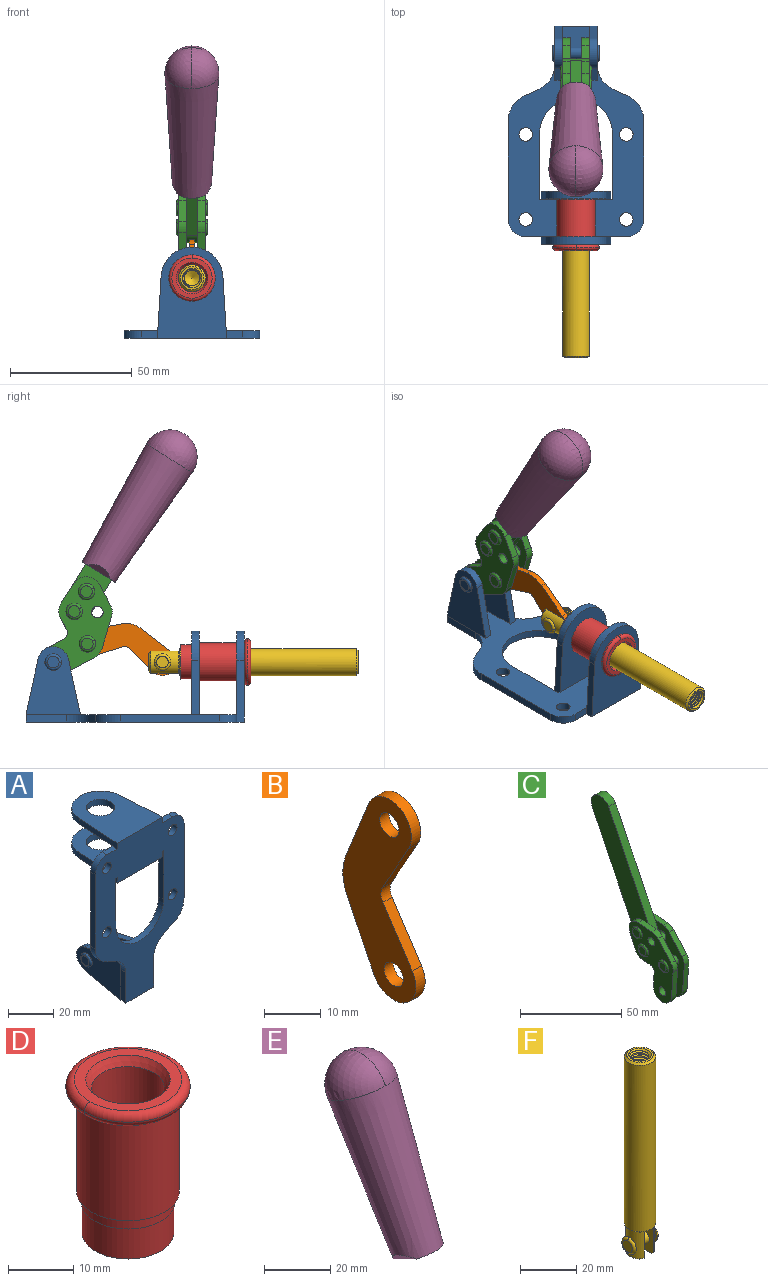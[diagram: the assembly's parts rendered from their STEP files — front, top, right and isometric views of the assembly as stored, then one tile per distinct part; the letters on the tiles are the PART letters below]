
ASSEMBLY  parts=6 mates=6
PART A: 55 faces, bbox 55.7x37.4x89.8 mm
  f0: torus R=2.41mm, axis (-1,0,0), area 15mm2, adj f11,f15,f25
  f1: torus R=2.41mm, axis (-1,0,0), area 15mm2, adj f10,f12,f22
  f2: cylinder r=2.78mm len=5.56mm, axis (0,-1,0), area 54.2mm2, adj f30,f54
  f3: cylinder r=14.99mm len=29.97mm, axis (0,-1,0), area 145.9mm2, adj f30,f49,f53,f54
  f4: cylinder r=2.78mm len=5.56mm, axis (0,-1,0), area 54.2mm2, adj f30,f54
  f5: cylinder r=2.78mm len=5.56mm, axis (0,-1,0), area 54.2mm2, adj f30,f54
  f6: cylinder r=2.78mm len=5.56mm, axis (0,-1,0), area 54.2mm2, adj f30,f54
  f7: cylinder r=6.35mm len=12.7mm, axis (0,0,1), area 123.6mm2, adj f27,f51
  f8: cylinder r=6.35mm len=12.7mm, axis (0,0,-1), area 124.7mm2, adj f21,f35
  f9: cylinder r=2.41mm len=11.18mm, axis (-1,0,0), area 169.4mm2, adj f16,f19
  f10: plane 4.83x4.83mm, normal (1,0,0), area 18.3mm2, adj f1,f12
  f11: plane 4.83x4.83mm, normal (-1,0,0), area 18.3mm2, adj f0,f15
  f12: torus R=2.41mm, axis (-1,0,0), area 15mm2, adj f1,f10,f22
  f13: cylinder r=6.35mm len=12.41mm, axis (1,0,0), area 53.4mm2, adj f18,f19,f22,f23
  f14: cylinder r=6.35mm len=12.41mm, axis (-1,0,0), area 53.4mm2, adj f16,f17,f24,f25
  f15: torus R=2.41mm, axis (-1,0,0), area 15mm2, adj f0,f11,f25
  f16: plane 27.86x22.35mm, normal (1,0,0), area 425.4mm2, adj f9,f14,f17,f24,f30
  f17: plane 22.86x4.97mm, normal (0,0.21,0.98), area 72.5mm2, adj f14,f16,f25,f30
  f18: plane 22.86x4.97mm, normal (0,0.21,0.98), area 72.5mm2, adj f13,f19,f22,f30
  f19: plane 27.86x22.35mm, normal (-1,0,0), area 425.4mm2, adj f9,f13,f18,f23,f30
  f20: cylinder r=12.7mm len=25.35mm, axis (0,0,-1), area 119.8mm2, adj f21,f34,f35,f36
  f21: plane 34.21x28.07mm, normal (0,0,-1), area 702.4mm2, adj f8,f20,f30,f34,f36
  f22: plane 27.96x22.45mm, normal (1,0,0), area 407.2mm2, adj f1,f12,f13,f18,f23,f30,f42,f43
  f23: plane 22.86x4.97mm, normal (0,0.21,-0.98), area 72.5mm2, adj f13,f19,f22,f44
  f24: plane 22.86x4.97mm, normal (0,0.21,-0.98), area 72.5mm2, adj f14,f16,f25,f44
  f25: plane 27.86x22.35mm, normal (-1,0,0), area 407.1mm2, adj f0,f14,f15,f17,f24,f30,f45,f46
  f26: plane 3.1x0.95mm, normal (0,0,-1), area 2.7mm2, adj f30,f49,f50,f54
  f27: plane 34.21x28.07mm, normal (0,0,1), area 702.4mm2, adj f7,f28,f30,f50,f52
  f28: cylinder r=12.7mm len=25.35mm, axis (0,0,1), area 118.8mm2, adj f27,f50,f51,f52
  f29: plane 3.1x0.95mm, normal (0,0,-1), area 2.7mm2, adj f30,f52,f53,f54
  f30: plane 86.54x55.63mm, normal (0,1,0), area 2362.9mm2, adj f2,f3,f4,f5,f6,f16,f17,f18
  f31: plane 40.56x3.1mm, normal (-1,0,0), area 125.7mm2, adj f30,f32,f48,f54
  f32: cylinder r=7.11mm len=7.11mm, axis (0,-1,0), area 34.6mm2, adj f30,f31,f33,f54
  f33: plane 6.67x3.1mm, normal (0,0,1), area 20.4mm2, adj f30,f32,f34,f54
  f34: plane 25.39x3.13mm, normal (-1,0.06,0), area 79.5mm2, adj f20,f21,f33,f35,f54
  f35: plane 37.31x28.45mm, normal (0,0,1), area 789.9mm2, adj f8,f20,f34,f36,f54
  f36: plane 25.39x3.13mm, normal (1,0.06,0), area 79.5mm2, adj f20,f21,f35,f37,f54
  f37: plane 6.67x3.1mm, normal (0,0,1), area 20.4mm2, adj f30,f36,f38,f54
  f38: cylinder r=7.11mm len=7.11mm, axis (0,-1,0), area 34.6mm2, adj f30,f37,f39,f54
  f39: plane 40.56x3.1mm, normal (1,0,0), area 125.7mm2, adj f30,f38,f40,f54
  f40: cylinder r=11.18mm len=10.16mm, axis (0,-1,0), area 39.5mm2, adj f30,f39,f41,f54
  f41: plane 6.09x3.1mm, normal (0.42,0,-0.91), area 20.8mm2, adj f30,f40,f42,f54
  f42: cylinder r=11.18mm len=9.41mm, axis (0,-1,0), area 37.2mm2, adj f22,f30,f41,f43,f54
  f43: plane 16.5x3.1mm, normal (1,0,0), area 51.1mm2, adj f22,f42,f44,f54
  f44: plane 17.37x3.1mm, normal (0,0,-1), area 53.8mm2, adj f23,f24,f30,f43,f45,f54
  f45: plane 16.5x3.1mm, normal (-1,0,0), area 51.1mm2, adj f25,f44,f46,f54
  f46: cylinder r=11.18mm len=9.41mm, axis (0,-1,0), area 37.2mm2, adj f25,f30,f45,f47,f54
  f47: plane 6.09x3.1mm, normal (-0.42,0,-0.91), area 20.8mm2, adj f30,f46,f48,f54
  f48: cylinder r=11.18mm len=10.16mm, axis (0,-1,0), area 39.5mm2, adj f30,f31,f47,f54
  f49: plane 26.54x3.1mm, normal (-1,0,0), area 82.3mm2, adj f3,f26,f30,f54
  f50: plane 25.39x3.1mm, normal (1,0.06,0), area 78.8mm2, adj f26,f27,f28,f51,f54
  f51: plane 37.31x28.45mm, normal (0,0,-1), area 789.9mm2, adj f7,f28,f50,f52,f54
  f52: plane 25.39x3.1mm, normal (-1,0.06,0), area 78.8mm2, adj f27,f28,f29,f51,f54
  f53: plane 26.54x3.1mm, normal (1,0,0), area 82.3mm2, adj f3,f29,f30,f54
  f54: plane 89.66x55.63mm, normal (0,-1,0), area 2678.5mm2, adj f2,f3,f4,f5,f6,f26,f29,f31
PART B: 12 faces, bbox 2.3x18.2x42.8 mm
  f0: cylinder r=2.4mm len=4.8mm, axis (1,0,0), area 34.9mm2, adj f4,f11
  f1: cylinder r=10.41mm len=8.47mm, axis (1,0,0), area 20.2mm2, adj f4,f9,f10,f11
  f2: cylinder r=3.05mm len=3.16mm, axis (1,0,0), area 7.7mm2, adj f4,f6,f7,f11
  f3: cylinder r=2.4mm len=4.8mm, axis (1,0,0), area 34.9mm2, adj f4,f11
  f4: plane 42.81x18.23mm, normal (-1,0,0), area 414.1mm2, adj f0,f1,f2,f3,f5,f6,f7,f8
  f5: cylinder r=5.54mm len=10.67mm, axis (1,0,0), area 41.8mm2, adj f4,f6,f10,f11
  f6: plane 11.66x6.53mm, normal (0,-0.87,-0.49), area 30.9mm2, adj f2,f4,f5,f11
  f7: plane 11.17x7.33mm, normal (0,-0.84,0.55), area 30.9mm2, adj f2,f4,f8,f11
  f8: cylinder r=5.54mm len=10.51mm, axis (1,0,0), area 41.8mm2, adj f4,f7,f9,f11
  f9: plane 13.67x6.67mm, normal (0,0.9,-0.44), area 35.1mm2, adj f1,f4,f8,f11
  f10: plane 14.1x5.7mm, normal (0,0.93,0.37), area 35.1mm2, adj f1,f4,f5,f11
  f11: plane 42.81x18.23mm, normal (1,0,0), area 414.1mm2, adj f0,f1,f2,f3,f5,f6,f7,f8
PART C: 59 faces, bbox 12.9x60.2x99.6 mm
  f0: torus R=2.39mm, axis (-1,0,0), area 14.9mm2, adj f20,f43,f51
  f1: torus R=2.39mm, axis (-1,0,0), area 14.9mm2, adj f19,f42,f51
  f2: torus R=2.39mm, axis (-1,0,0), area 14.9mm2, adj f18,f35,f51
  f3: torus R=2.39mm, axis (-1,0,0), area 14.9mm2, adj f14,f17,f23
  f4: torus R=2.39mm, axis (-1,0,0), area 14.9mm2, adj f13,f16,f23
  f5: torus R=2.39mm, axis (-1,0,0), area 14.9mm2, adj f12,f15,f23
  f6: cylinder r=2.39mm len=4.78mm, axis (1,0,0), area 46.5mm2, adj f48,f50,f51
  f7: cylinder r=2.39mm len=4.78mm, axis (1,0,0), area 46.5mm2, adj f50,f51
  f8: cylinder r=6.35mm len=12.68mm, axis (1,0,0), area 61.8mm2, adj f38,f39,f50,f51
  f9: cylinder r=2.39mm len=4.78mm, axis (-1,0,0), area 70.5mm2, adj f46,f50
  f10: cylinder r=2.39mm len=4.78mm, axis (-1,0,0), area 46.5mm2, adj f23,f45,f46
  f11: cylinder r=2.39mm len=4.78mm, axis (-1,0,0), area 46.5mm2, adj f23,f46
  f12: plane 4.78x4.78mm, normal (1,0,0), area 17.9mm2, adj f5,f15
  f13: plane 4.78x4.78mm, normal (1,0,0), area 17.9mm2, adj f4,f16
  f14: plane 4.78x4.78mm, normal (1,0,0), area 17.9mm2, adj f3,f17
  f15: torus R=2.39mm, axis (-1,0,0), area 14.9mm2, adj f5,f12,f23
  f16: torus R=2.39mm, axis (-1,0,0), area 14.9mm2, adj f4,f13,f23
  f17: torus R=2.39mm, axis (-1,0,0), area 14.9mm2, adj f3,f14,f23
  f18: plane 4.78x4.78mm, normal (-1,0,0), area 17.9mm2, adj f2,f35
  f19: plane 4.78x4.78mm, normal (-1,0,0), area 17.9mm2, adj f1,f42
  f20: plane 4.78x4.78mm, normal (-1,0,0), area 17.9mm2, adj f0,f43
  f21: plane 2.26x0.2mm, normal (1,0,0), area 0.2mm2, adj f31,f44
  f22: plane 2.26x0.2mm, normal (-1,0,0), area 0.2mm2, adj f41,f44
  f23: plane 39.37x30.77mm, normal (1,0,0), area 565.5mm2, adj f3,f4,f5,f10,f11,f15,f16,f17
  f24: cylinder r=6.1mm len=4.15mm, axis (-1,0,0), area 14.7mm2, adj f23,f25,f32,f46
  f25: plane 10.25x9.01mm, normal (0,-0.75,0.66), area 42.3mm2, adj f23,f24,f26,f46
  f26: cylinder r=6.35mm len=4.64mm, axis (-1,0,0), area 15.6mm2, adj f23,f25,f27,f46
  f27: plane 15.84x3.1mm, normal (0,-1,-0.07), area 49.2mm2, adj f23,f26,f28,f46
  f28: cylinder r=6.35mm len=12.68mm, axis (-1,0,0), area 61.8mm2, adj f23,f27,f29,f46
  f29: plane 8.11x3.1mm, normal (0,1,0.07), area 25.2mm2, adj f23,f28,f30,f46
  f30: cylinder r=3.05mm len=3.25mm, axis (-1,0,0), area 14.8mm2, adj f23,f29,f31,f46
  f31: plane 5.99x3.1mm, normal (0,0.07,-1), area 18.6mm2, adj f21,f23,f30,f44,f46
  f32: plane 9.5x3.1mm, normal (0,-0.07,1), area 29.5mm2, adj f23,f24,f33,f46,f47
  f33: cylinder r=6.1mm len=8.63mm, axis (-1,0,0), area 39.1mm2, adj f23,f32,f34,f47
  f34: plane 8.65x3.96mm, normal (0,0.91,-0.42), area 29.5mm2, adj f23,f33,f44,f47
  f35: torus R=2.39mm, axis (-1,0,0), area 14.9mm2, adj f2,f18,f51
  f36: plane 10.25x9.01mm, normal (0,-0.75,0.66), area 42.3mm2, adj f37,f49,f50,f51
  f37: cylinder r=6.35mm len=4.64mm, axis (1,0,0), area 15.6mm2, adj f36,f38,f50,f51
  f38: plane 15.84x3.1mm, normal (0,-1,-0.07), area 49.2mm2, adj f8,f37,f50,f51
  f39: plane 8.11x3.1mm, normal (0,1,0.07), area 25.2mm2, adj f8,f40,f50,f51
  f40: cylinder r=3.05mm len=3.25mm, axis (1,0,0), area 14.8mm2, adj f39,f41,f50,f51
  f41: plane 5.99x3.1mm, normal (0,0.07,-1), area 18.6mm2, adj f22,f40,f44,f50,f51
  f42: torus R=2.39mm, axis (-1,0,0), area 14.9mm2, adj f1,f19,f51
  f43: torus R=2.39mm, axis (-1,0,0), area 14.9mm2, adj f0,f20,f51
  f44: cylinder r=6.35mm len=12.12mm, axis (-1,0,0), area 128.9mm2, adj f21,f22,f23,f31,f34,f41,f46,f47
  f45: plane 2.65x1.35mm, normal (1,0,0), area 1mm2, adj f10,f55
  f46: plane 39.08x20.42mm, normal (-1,0,0), area 412.5mm2, adj f9,f10,f11,f24,f25,f26,f27,f28
  f47: plane 77.62x39.82mm, normal (1,0,0), area 850mm2, adj f32,f33,f34,f44,f53,f54,f55
  f48: plane 2.65x1.35mm, normal (-1,0,0), area 1mm2, adj f6,f55
  f49: cylinder r=6.1mm len=4.15mm, axis (1,0,0), area 14.7mm2, adj f36,f50,f51,f56
  f50: plane 39.08x20.42mm, normal (1,0,0), area 412.5mm2, adj f6,f7,f8,f9,f36,f37,f38,f39
  f51: plane 39.37x30.77mm, normal (-1,0,0), area 565.5mm2, adj f0,f1,f2,f6,f7,f8,f35,f36
  f52: plane 8.65x3.96mm, normal (0,0.91,-0.42), area 29.5mm2, adj f44,f51,f57,f58
  f53: plane 68.49x33.4mm, normal (0,0.9,-0.44), area 358.1mm2, adj f44,f47,f54,f58
  f54: cylinder r=6.35mm len=12.06mm, axis (1,0,0), area 93.7mm2, adj f47,f53,f55,f58
  f55: plane 68.49x33.4mm, normal (0,-0.9,0.44), area 358.1mm2, adj f44,f45,f46,f47,f48,f50,f54,f58
  f56: plane 9.5x3.1mm, normal (0,-0.07,1), area 29.5mm2, adj f49,f50,f51,f57,f58
  f57: cylinder r=6.1mm len=8.63mm, axis (1,0,0), area 39.1mm2, adj f51,f52,f56,f58
  f58: plane 77.62x39.82mm, normal (-1,0,0), area 850mm2, adj f44,f52,f53,f54,f55,f56,f57
PART D: 15 faces, bbox 20.6x20.6x28.7 mm
  f0: torus R=8.26mm, axis (0,0,1), area 56.8mm2, adj f1,f10,f12
  f1: torus R=8.26mm, axis (0,0,1), area 56.8mm2, adj f0,f6,f13
  f2: cylinder r=5.59mm len=25.91mm, axis (0,0,1), area 909.6mm2, adj f3,f4
  f3: cone r=6.86mm half-angle=45deg, axis (0,0,-1), area 70.2mm2, adj f2,f14
  f4: cone r=6.47mm half-angle=30deg, axis (0,0,1), area 66.7mm2, adj f2,f13
  f5: cylinder r=7.04mm len=14.07mm, axis (0,0,1), area 252.6mm2, adj f11,f14
  f6: torus R=8.26mm, axis (0,0,1), area 56.8mm2, adj f1,f12,f13
  f7: cylinder r=7.16mm len=14.33mm, axis (0,0,1), area 91.5mm2, adj f9,f11
  f8: cylinder r=7.86mm len=18.42mm, axis (0,0,1), area 909.6mm2, adj f9,f10
  f9: plane 15.72x15.72mm, normal (0,0,-1), area 33mm2, adj f7,f8
  f10: plane 16.51x16.51mm, normal (0,0,-1), area 19.9mm2, adj f0,f8,f12
  f11: plane 14.33x14.33mm, normal (0,0,-1), area 5.7mm2, adj f5,f7
  f12: torus R=8.26mm, axis (0,0,1), area 56.8mm2, adj f0,f6,f10
  f13: plane 16.51x16.51mm, normal (0,0,1), area 82.7mm2, adj f1,f4,f6
  f14: plane 14.07x14.07mm, normal (0,0,-1), area 7.8mm2, adj f3,f5
PART E: 11 faces, bbox 22.3x42.6x64.5 mm
  f0: sphere r=11.13mm, area 411.4mm2, adj f1,f8
  f1: cone r=11.11mm half-angle=3.3deg, axis (0,0.44,0.9), area 3251.8mm2, adj f0,f7,f8,f9,f10
  f2: cylinder r=6.16mm len=11.7mm, axis (1,0,0), area 89.5mm2, adj f3,f4,f5,f6
  f3: plane 60.23x36.75mm, normal (-1,0,0), area 763.6mm2, adj f2,f4,f6,f10
  f4: plane 51.37x25.05mm, normal (0,0.9,-0.44), area 264.2mm2, adj f2,f3,f5,f10
  f5: plane 60.23x36.75mm, normal (1,0,0), area 763.6mm2, adj f2,f4,f6,f10
  f6: plane 51.37x25.05mm, normal (0,-0.9,0.44), area 264.2mm2, adj f2,f3,f5,f10
  f7: plane 9.95x5.95mm, normal (0.71,-0.31,-0.64), area 25.8mm2, adj f1,f10
  f8: sphere r=11.13mm, area 411.4mm2, adj f0,f1
  f9: plane 9.95x5.95mm, normal (-0.71,-0.31,-0.64), area 25.8mm2, adj f1,f10
  f10: plane 14.27x11.38mm, normal (0,-0.44,-0.9), area 106.7mm2, adj f1,f3,f4,f5,f6,f7,f9
PART F: 48 faces, bbox 12.6x11.1x86.1 mm
  f0: torus R=2.41mm, axis (-1,0,0), area 15mm2, adj f30,f32,f34
  f1: torus R=2.41mm, axis (-1,0,0), area 15mm2, adj f29,f31,f33
  f2: cylinder r=5.54mm len=72.39mm, axis (0,0,1), area 2518.5mm2, adj f3,f4,f42,f43
  f3: cone r=5.54mm half-angle=45deg, axis (0,0,1), area 7.6mm2, adj f2,f5,f41
  f4: cone r=5.54mm half-angle=45deg, axis (0,0,-1), area 34.9mm2, adj f2,f39
  f5: cylinder r=5.08mm len=11.48mm, axis (0,0,1), area 108.3mm2, adj f3,f7,f8,f41
  f6: cylinder r=2.41mm len=4.83mm, axis (-1,0,0), area 71.2mm2, adj f40,f41
  f7: cylinder r=2.41mm len=4.83mm, axis (-1,0,0), area 7.6mm2, adj f5,f34
  f8: cone r=5.08mm half-angle=45deg, axis (0,0,1), area 10.6mm2, adj f5,f37,f41
  f9: cone r=3.98mm half-angle=45deg, axis (0,0,1), area 17.6mm2, adj f27,f39,f45,f46,f47
  f10: cylinder r=2.41mm len=4.83mm, axis (-1,0,0), area 7.6mm2, adj f33,f38
  f11: cylinder r=3.2mm len=6.4mm, axis (0,0,1), area 78.4mm2, adj f12,f28,f44,f45,f47
  f12: cylinder r=3.2mm len=6.4mm, axis (0,0,1), area 10.5mm2, adj f11,f13,f45,f47
  f13: cylinder r=3.2mm len=6.4mm, axis (0,0,1), area 10.5mm2, adj f12,f14,f45,f47
  f14: cylinder r=3.2mm len=6.4mm, axis (0,0,1), area 10.5mm2, adj f13,f15,f45,f47
  f15: cylinder r=3.2mm len=6.4mm, axis (0,0,1), area 10.5mm2, adj f14,f16,f45,f47
  f16: cylinder r=3.2mm len=6.4mm, axis (0,0,1), area 10.5mm2, adj f15,f17,f45,f47
  f17: cylinder r=3.2mm len=6.4mm, axis (0,0,1), area 10.5mm2, adj f16,f18,f45,f47
  f18: cylinder r=3.2mm len=6.4mm, axis (0,0,1), area 10.5mm2, adj f17,f19,f45,f47
  f19: cylinder r=3.2mm len=6.4mm, axis (0,0,1), area 10.5mm2, adj f18,f20,f45,f47
  f20: cylinder r=3.2mm len=6.4mm, axis (0,0,1), area 10.5mm2, adj f19,f21,f45,f47
  f21: cylinder r=3.2mm len=6.4mm, axis (0,0,1), area 10.5mm2, adj f20,f22,f45,f47
  f22: cylinder r=3.2mm len=6.4mm, axis (0,0,1), area 10.5mm2, adj f21,f23,f45,f47
  f23: cylinder r=3.2mm len=6.4mm, axis (0,0,1), area 10.5mm2, adj f22,f24,f45,f47
  f24: cylinder r=3.2mm len=6.4mm, axis (0,0,1), area 10.5mm2, adj f23,f25,f45,f47
  f25: cylinder r=3.2mm len=6.4mm, axis (0,0,1), area 10.5mm2, adj f24,f26,f45,f47
  f26: cylinder r=3.2mm len=6.4mm, axis (0,0,1), area 10.5mm2, adj f25,f27,f45,f47
  f27: cylinder r=3.2mm len=6.4mm, axis (0,0,1), area 7.4mm2, adj f9,f26,f45,f47
  f28: cone r=3.2mm half-angle=60deg, axis (0,0,1), area 37.2mm2, adj f11
  f29: plane 4.83x4.83mm, normal (-1,0,0), area 18.3mm2, adj f1,f31
  f30: plane 4.83x4.83mm, normal (1,0,0), area 18.3mm2, adj f0,f32
  f31: torus R=2.41mm, axis (-1,0,0), area 15mm2, adj f1,f29,f33
  f32: torus R=2.41mm, axis (-1,0,0), area 15mm2, adj f0,f30,f34
  f33: plane 6.83x6.83mm, normal (1,0,0), area 18.3mm2, adj f1,f10,f31
  f34: plane 6.83x6.83mm, normal (-1,0,0), area 18.3mm2, adj f0,f7,f32
  f35: cone r=5.08mm half-angle=45deg, axis (0,0,1), area 10.6mm2, adj f36,f38,f40
  f36: plane 7.25x1.97mm, normal (0,0,-1), area 10mm2, adj f35,f40
  f37: plane 7.25x1.97mm, normal (0,0,-1), area 10mm2, adj f8,f41
  f38: cylinder r=5.08mm len=11.48mm, axis (0,0,1), area 108.3mm2, adj f10,f35,f40,f42
  f39: plane 9.55x9.55mm, normal (0,0,1), area 22mm2, adj f4,f9
  f40: plane 12.76x10.09mm, normal (1,0,0), area 95.7mm2, adj f6,f35,f36,f38,f42,f43
  f41: plane 12.76x10.09mm, normal (-1,0,0), area 95.7mm2, adj f3,f5,f6,f8,f37,f43
  f42: cone r=5.54mm half-angle=45deg, axis (0,0,1), area 7.6mm2, adj f2,f38,f40
  f43: plane 11.07x4.7mm, normal (0,0,-1), area 50.4mm2, adj f2,f40,f41
  f44: plane 0.89x0.62mm, normal (-1,0,0), area 0.3mm2, adj f11,f45,f46,f47
  f45: bspline ~24.8x7.63mm, area 266.6mm2, adj f9,f11,f12,f13,f14,f15,f16,f17
  f46: bspline ~24.87x7.63mm, area 73.6mm2, adj f9,f44,f45,f47
  f47: bspline ~24.98x7.63mm, area 272.5mm2, adj f9,f11,f12,f13,f14,f15,f16,f17
PLACE A rot(axis=(1,0,0),90deg) t=(0,9.43,0)mm fixed
PLACE B rot(axis=(1,0,0),105.7deg) t=(0,18.22,5.09)mm
PLACE C rot(axis=(1,0,0),57.8deg) t=(0,1.25,20.87)mm
PLACE D rot(axis=(0.58,-0.58,0.58),120deg) t=(24.61,9.43,24.61)mm
PLACE E rot(axis=(1,0,0),57.8deg) t=(-0.04,1.25,20.87)mm
PLACE F rot(axis=(1,0,0),90deg) t=(0,12.15,0)mm
MATE revolute A.f0 <-> C.f7  axis (-1,0,0) through (0,41.52,24.61)mm
MATE fastened D.f2 <-> A.f7  axis (0,1,0) through (0,-36.96,24.61)mm
MATE fastened E.f2 <-> C.f54  axis (1,0,0) through (-2.35,-7.28,110.17)mm
MATE revolute B.f5 <-> F.f6  axis (1,0,0) through (0,-3.32,24.61)mm
MATE revolute B.f3 <-> C.f4  axis (1,0,0) through (0,27.53,32.11)mm
MATE slider F.f2 <-> D.f2  axis (0,-1,0) through (0,-46.63,24.61)mm
